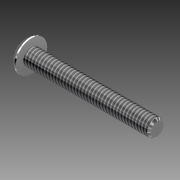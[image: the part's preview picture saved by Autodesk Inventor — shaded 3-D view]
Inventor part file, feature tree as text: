
AUTODESK INVENTOR PART (.ipt)
format: ipt  version: 2011 (Build 150239000, 239)  size: 107,520 bytes
history: native  units: in
note: dims shown in document units (in); Inventor stores cm internally (conversion verified against a paired STEP export)
features: other x1, imported_body x1, thread x1
ambient origin geometry x8: Origin, YZ Plane, XZ Plane, XY Plane, X Axis, Y Axis, Z Axis, Center Point
feature tree (3):
  parser-record x1  (decoder bookkeeping rows leaked as tree rows — omitted from the tree; the rows remain in map.json)
  imported_body  "Base1"
  thread  "Thread1"  [1 undecoded]
note: 1 required parameter value undecoded (feature->parameter linkage not recoverable at this tier; creation-order binding heuristic only, values carry confidence <= 0.55)
